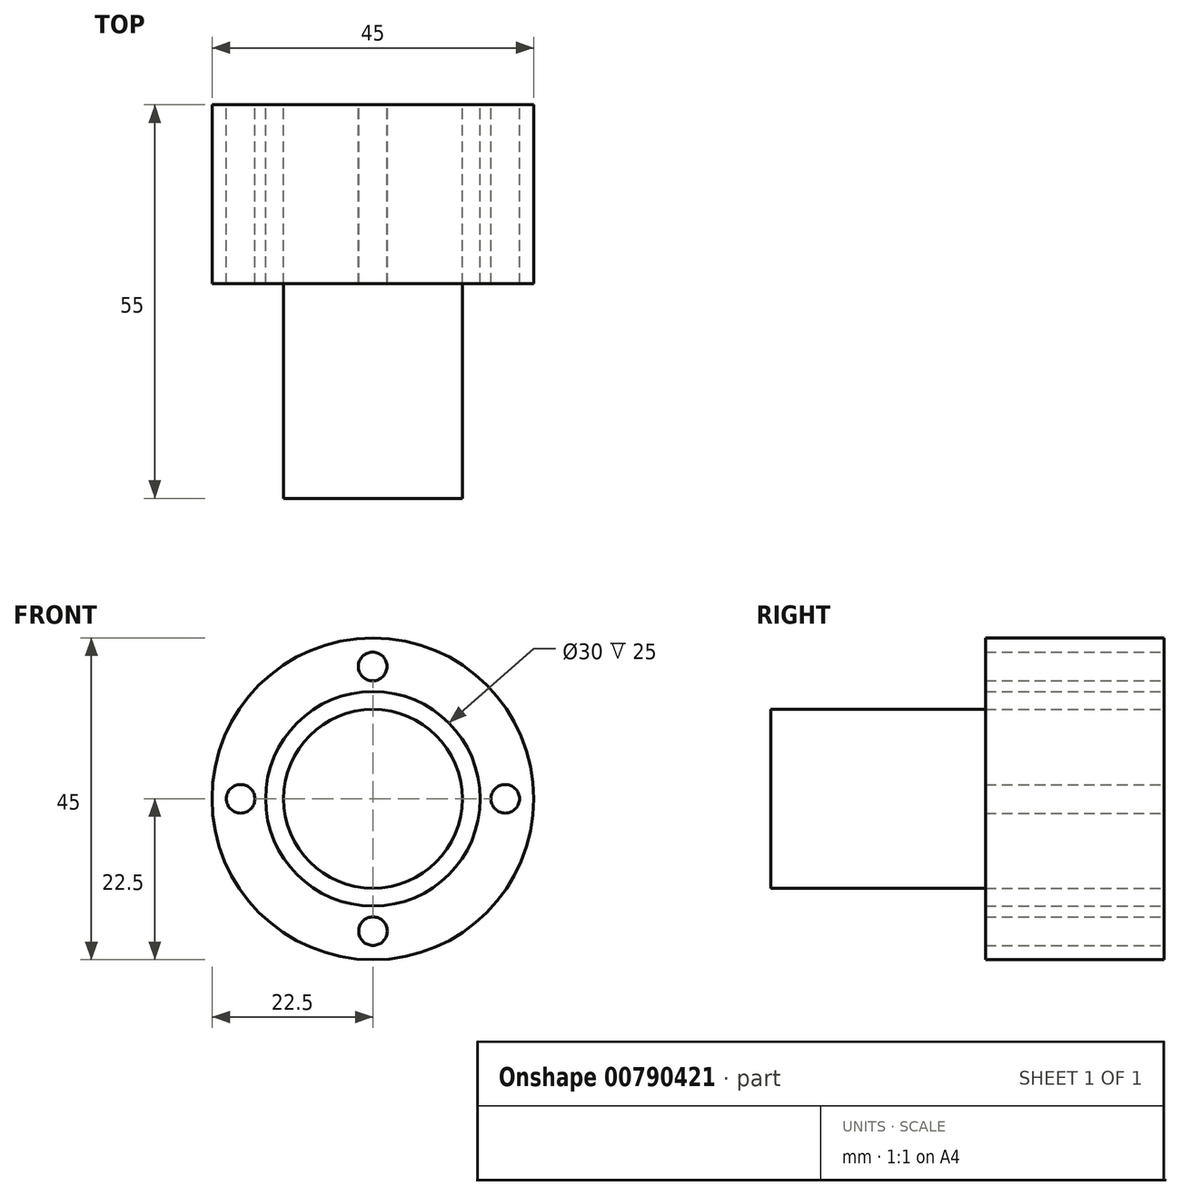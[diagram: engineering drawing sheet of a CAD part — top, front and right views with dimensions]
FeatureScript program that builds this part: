
annotation { "Feature Type Name" : "Feature", "Feature Type Description" : "" }
export const myFeature = defineFeature(function(context is Context, id is Id, definition is map)
    precondition{}
    {
        {
            var Q0;
            Q0=qCreatedBy(makeId("Front.planeOp"),FACE);
            var sketch = newSketch(context, id + "F0", { "sketchPlane" : qUnion([Q0])});
            skCircle(sketch, "E0", {"center": v(0, 0) * mm, "radius": 15 * mm});
            skCircle(sketch, "E1", {"center": v(0, 0) * mm, "radius": 22.5 * mm});
            skCircle(sketch, "E2", {"center": v(0, 0) * mm, "radius": 12.5 * mm});
            skCircle(sketch, "E3", {"center": v(-18.5, 0) * mm, "radius": 2 * mm});
            skCircle(sketch, "E4", {"center": v(18.5, 0) * mm, "radius": 2 * mm});
            skCircle(sketch, "E5", {"center": v(0, -18.5) * mm, "radius": 2 * mm});
            skCircle(sketch, "E6", {"center": v(-0.04, 18.5) * mm, "radius": 2 * mm});
            skSolve(sketch);
        }
        {
            var Q0;
            Q0=makeQuery(id+"F0.imprint","IMPRINT",FACE,{"disambiguationData":[TD([[makeQuery(id+"F0.imprint","IMPRINT",EDGE,{"derivedFrom":sQuery(id+"F0.wireOp",EDGE,"E0")}),-1.0]])]});
            var Q1;
            Q1=makeQuery(id+"F0.imprint","IMPRINT",FACE,{"disambiguationData":[TD([[makeQuery(id+"F0.imprint","IMPRINT",EDGE,{"derivedFrom":sQuery(id+"F0.wireOp",EDGE,"E2")}),1.0]])]});
            extrude(context, id + "F1", {"entities" : qUnion([Q0, Q1]), "depth" : 25 * mm, "offsetDistance" : 25 * mm});
        }
        {
            var Q0;
            Q0=makeQuery(id+"F1.opExtrude","CAP_FACE",FACE,{"disambiguationData":[OSD([sQuery(id+"F0.wireOp",EDGE,"E2")])],"isStart":false});
            var Q1;
            Q1=makeQuery(id+"F1.opExtrude","CAP_FACE",FACE,{"disambiguationData":[OSD([sQuery(id+"F0.wireOp",EDGE,"E2")])],"isStart":true});
            extrude(context, id + "F2", {"entities" : qUnion([Q0, Q1]), "operationType" : NewBodyOperationType.ADD, "depth" : 30 * mm, "offsetDistance" : 25 * mm});
        }
    });
